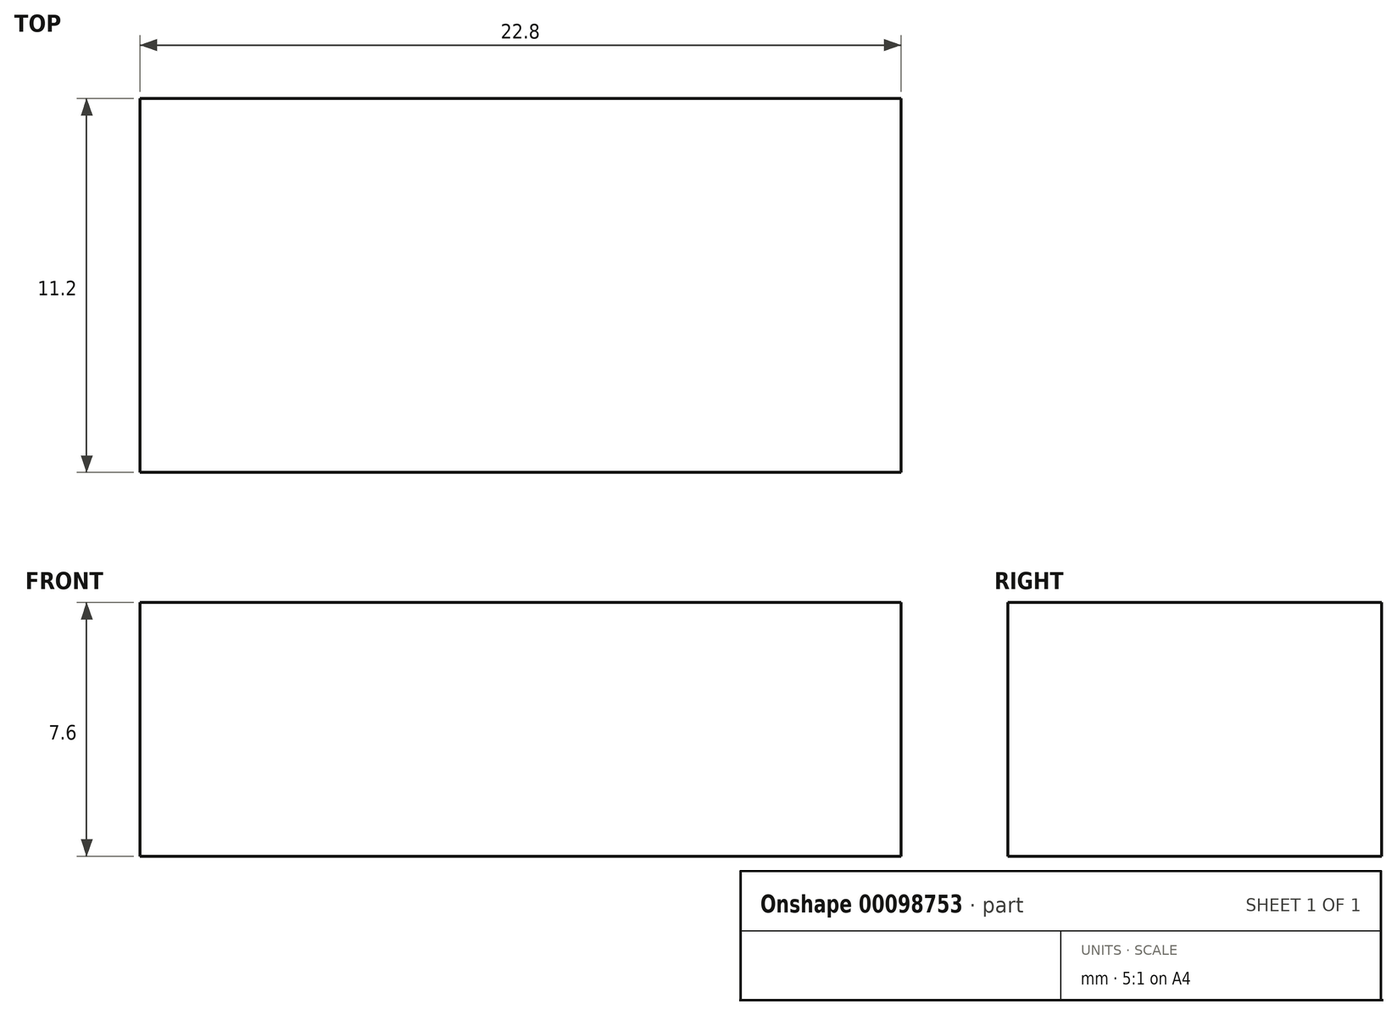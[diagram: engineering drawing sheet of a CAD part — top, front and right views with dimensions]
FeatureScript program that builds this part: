
annotation { "Feature Type Name" : "Feature", "Feature Type Description" : "" }
export const myFeature = defineFeature(function(context is Context, id is Id, definition is map)
    precondition{}
    {
        {
            var Q0;
            Q0=qCreatedBy(makeId("Front.planeOp"),FACE);
            var sketch = newSketch(context, id + "F0", { "sketchPlane" : qUnion([Q0])});
            skLineSegment(sketch, "E0", {"start": v(0, 0) * mm, "end": v(0, 7.6) * mm});
            skLineSegment(sketch, "E1", {"start": v(0, 7.6) * mm, "end": v(-22.8, 7.6) * mm});
            skLineSegment(sketch, "E2", {"start": v(-22.8, 7.6) * mm, "end": v(-22.8, 0) * mm});
            skLineSegment(sketch, "E3", {"start": v(-22.8, 0) * mm, "end": v(0, 0) * mm});
            skSolve(sketch);
        }
        {
            var Q0;
            Q0 = qSketchRegion(id + "F0", true);
            extrude(context, id + "F1", {"entities" : qUnion([Q0]), "depth" : 11.2 * mm});
        }
    });
